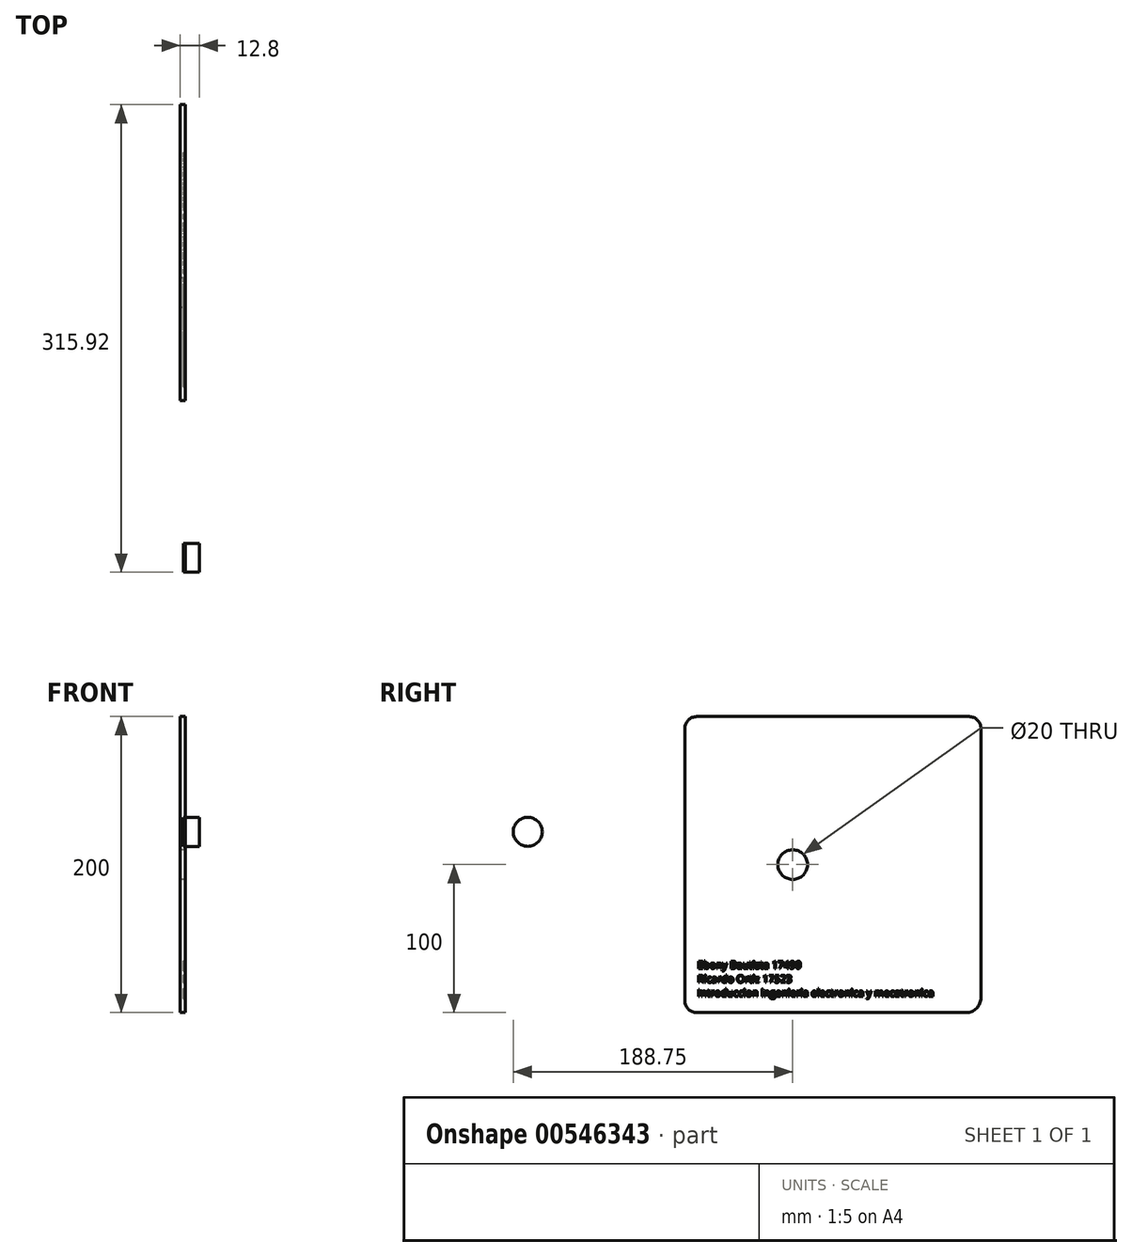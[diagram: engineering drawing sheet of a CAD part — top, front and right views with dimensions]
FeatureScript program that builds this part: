
annotation { "Feature Type Name" : "Feature", "Feature Type Description" : "" }
export const myFeature = defineFeature(function(context is Context, id is Id, definition is map)
    precondition{}
    {
        {
            var Q0;
            Q0=qCreatedBy(makeId("Right.planeOp"),FACE);
            var sketch = newSketch(context, id + "F0", { "sketchPlane" : qUnion([Q0])});
            skLineSegment(sketch, "E0.bottom", {"start": v(-118, 100) * mm, "end": v(82, 100) * mm});
            skLineSegment(sketch, "E0.top", {"start": v(-118, -100) * mm, "end": v(82, -100) * mm});
            skLineSegment(sketch, "E0.left", {"start": v(-118, 100) * mm, "end": v(-118, -100) * mm});
            skLineSegment(sketch, "E0.right", {"start": v(82, 100) * mm, "end": v(82, -100) * mm});
            skCircle(sketch, "E1", {"center": v(-45.17, 0) * mm, "radius": 10 * mm});
            skSolve(sketch);
        }
        {
            var Q0;
            Q0 = qSketchRegion(id + "F0", true);
            extrude(context, id + "F1", {"entities" : qUnion([Q0]), "depth" : 3.2 * mm, "offsetDistance" : 25 * mm});
        }
        {
            var Q0;
            Q0=makeQuery(id+"F1.opExtrude","SWEPT_EDGE",EDGE,{"disambiguationData":[OSD([sQuery(id+"F0.wireOp",EDGE,"E0.bottom"),sQuery(id+"F0.wireOp",EDGE,"E0.left")])]});
            var Q1;
            Q1=makeQuery(id+"F1.opExtrude","SWEPT_EDGE",EDGE,{"disambiguationData":[OSD([sQuery(id+"F0.wireOp",EDGE,"E0.top"),sQuery(id+"F0.wireOp",EDGE,"E0.left")])]});
            var Q2;
            Q2=makeQuery(id+"F1.opExtrude","SWEPT_EDGE",EDGE,{"disambiguationData":[OSD([sQuery(id+"F0.wireOp",EDGE,"E0.bottom"),sQuery(id+"F0.wireOp",EDGE,"E0.right")])]});
            fillet(context, id + "F2", {"entities" : qUnion([Q0, Q1, Q2]), "radius" : 8 * mm, "tangentPropagation" : true, "allowEdgeOverflow" : false});
        }
        {
            var Q0;
            Q0=makeQuery(id+"F1.opExtrude","CAP_FACE",FACE,{"disambiguationData":[OSD([sQuery(id+"F0.wireOp",EDGE,"E0.bottom"),sQuery(id+"F0.wireOp",EDGE,"E0.top"),sQuery(id+"F0.wireOp",EDGE,"E0.left"),sQuery(id+"F0.wireOp",EDGE,"E0.right"),sQuery(id+"F0.wireOp",EDGE,"E1")])],"isStart":false});
            var sketch = newSketch(context, id + "F3", { "sketchPlane" : qUnion([Q0])});
            skCircle(sketch, "E2", {"center": v(-224.12, 22.14) * mm, "radius": 9.8 * mm});
            skText(sketch, "E3", { "text": "Ebony Bautista 17490\nRicardo Ortiz 17523\nIntroduccion ingenieria electronica y mecatronica", "fontName": "OpenSans-Regular.ttf"});
            const initialGuessF3  = {"E3": [-0.1094, -0.07023, 1, 0, 0.005]};
            skSetInitialGuess(sketch, initialGuessF3);
            skSolve(sketch);
        }
        {
            var Q0;
            Q0=makeQuery(id+"F3.imprint","IMPRINT",FACE,{"disambiguationData":[TD([[makeQuery(id+"F3.imprint","IMPRINT",EDGE,{"derivedFrom":sQuery(id+"F3.wireOp",EDGE,"E2")}),1.0]])]});
            extrude(context, id + "F4", {"entities" : qUnion([Q0]), "depth" : 9.6 * mm, "offsetDistance" : 25 * mm});
        }
        {
            var Q0;
            Q0=makeQuery(id+"F1.opExtrude","SWEPT_EDGE",EDGE,{"disambiguationData":[OSD([sQuery(id+"F0.wireOp",EDGE,"E0.top"),sQuery(id+"F0.wireOp",EDGE,"E0.right")])]});
            fillet(context, id + "F5", {"entities" : qUnion([Q0]), "radius" : 10 * mm, "tangentPropagation" : true, "allowEdgeOverflow" : false});
        }
        {
            var Q0;
            Q0 = qSketchRegion(id + "F3", true);
            extrude(context, id + "F6", {"entities" : qUnion([Q0]), "oppositeDirection" : true, "depth" : 1 * mm, "offsetDistance" : 25 * mm});
        }
    });
